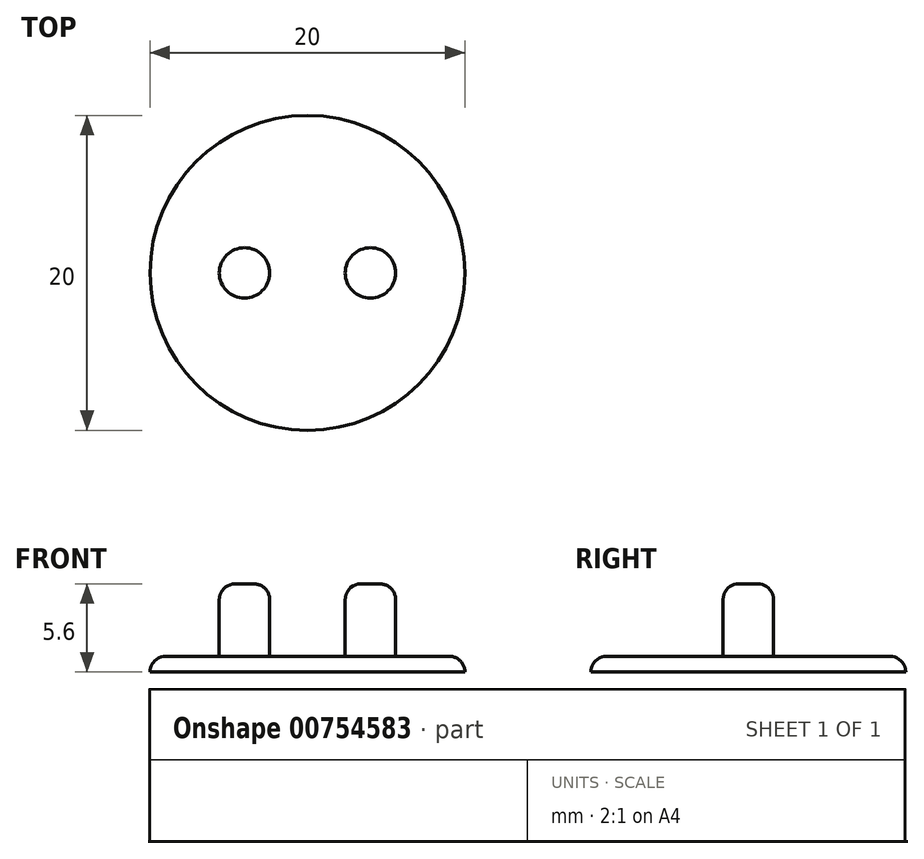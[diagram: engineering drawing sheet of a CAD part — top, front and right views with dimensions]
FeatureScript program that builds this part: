
annotation { "Feature Type Name" : "Feature", "Feature Type Description" : "" }
export const myFeature = defineFeature(function(context is Context, id is Id, definition is map)
    precondition{}
    {
        {
            var Q0;
            Q0=qCreatedBy(makeId("Top.planeOp"),FACE);
            var sketch = newSketch(context, id + "F0", { "sketchPlane" : qUnion([Q0])});
            skCircle(sketch, "E0", {"center": v(0, 0) * mm, "radius": 10 * mm});
            skCircle(sketch, "E1", {"center": v(-4, 0) * mm, "radius": 1.6 * mm});
            skCircle(sketch, "E2", {"center": v(4, 0) * mm, "radius": 1.6 * mm});
            skSolve(sketch);
        }
        {
            var Q0;
            Q0=makeQuery(id+"F0.imprint","IMPRINT",FACE,{"disambiguationData":[TD([[makeQuery(id+"F0.imprint","IMPRINT",EDGE,{"derivedFrom":sQuery(id+"F0.wireOp",EDGE,"E0")}),1.0]])]});
            var Q1;
            Q1=makeQuery(id+"F0.imprint","IMPRINT",FACE,{"disambiguationData":[TD([[makeQuery(id+"F0.imprint","IMPRINT",EDGE,{"derivedFrom":sQuery(id+"F0.wireOp",EDGE,"E1")}),1.0]])]});
            var Q2;
            Q2=makeQuery(id+"F0.imprint","IMPRINT",FACE,{"disambiguationData":[TD([[makeQuery(id+"F0.imprint","IMPRINT",EDGE,{"derivedFrom":sQuery(id+"F0.wireOp",EDGE,"E2")}),1.0]])]});
            extrude(context, id + "F1", {"entities" : qUnion([Q0, Q1, Q2]), "oppositeDirection" : true, "depth" : 1 * mm, "offsetDistance" : 25 * mm});
        }
        {
            var Q0;
            Q0=makeQuery(id+"F0.imprint","IMPRINT",FACE,{"disambiguationData":[TD([[makeQuery(id+"F0.imprint","IMPRINT",EDGE,{"derivedFrom":sQuery(id+"F0.wireOp",EDGE,"E1")}),1.0]])]});
            var Q1;
            Q1=makeQuery(id+"F0.imprint","IMPRINT",FACE,{"disambiguationData":[TD([[makeQuery(id+"F0.imprint","IMPRINT",EDGE,{"derivedFrom":sQuery(id+"F0.wireOp",EDGE,"E2")}),1.0]])]});
            extrude(context, id + "F2", {"entities" : qUnion([Q0, Q1]), "operationType" : NewBodyOperationType.ADD, "depth" : 4.6 * mm, "offsetDistance" : 25 * mm});
        }
        {
            var Q0;
            Q0=makeQuery(id+"F2.opExtrude","CAP_EDGE",EDGE,{"disambiguationData":[OSD([sQuery(id+"F0.wireOp",EDGE,"E1")])],"isStart":false});
            var Q1;
            Q1=makeQuery(id+"F2.opExtrude","CAP_EDGE",EDGE,{"disambiguationData":[OSD([sQuery(id+"F0.wireOp",EDGE,"E2")])],"isStart":false});
            fillet(context, id + "F3", {"entities" : qUnion([Q0, Q1]), "radius" : 1 * mm, "tangentPropagation" : true, "allowEdgeOverflow" : false});
        }
        {
            var Q0;
            Q0=makeQuery(id+"F1.opExtrude","CAP_EDGE",EDGE,{"disambiguationData":[OSD([sQuery(id+"F0.wireOp",EDGE,"E0")])],"isStart":true});
            fillet(context, id + "F4", {"entities" : qUnion([Q0]), "radius" : 1 * mm, "tangentPropagation" : true, "allowEdgeOverflow" : false});
        }
    });
